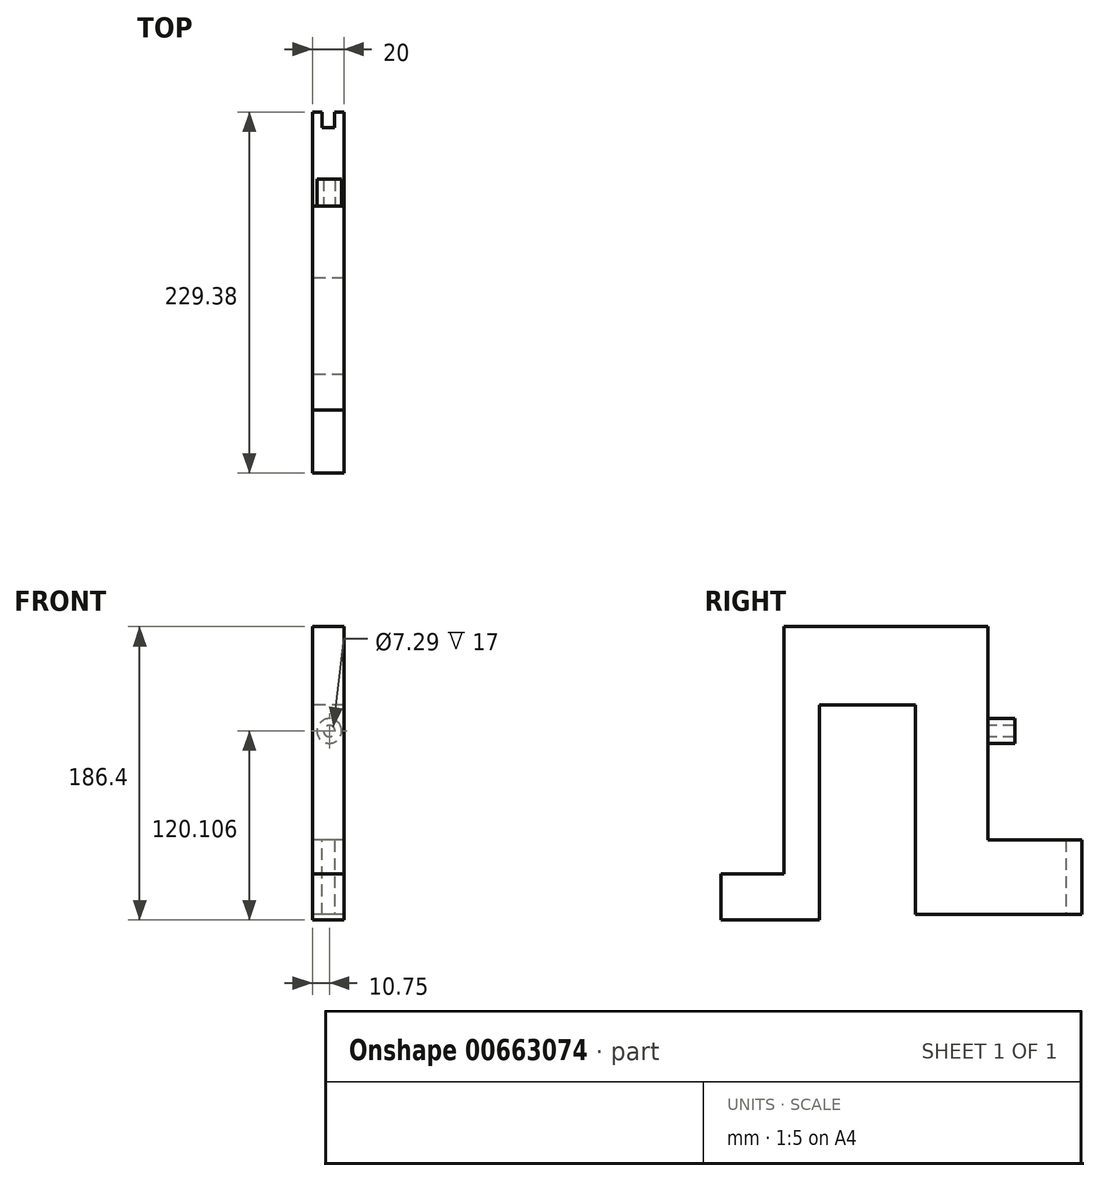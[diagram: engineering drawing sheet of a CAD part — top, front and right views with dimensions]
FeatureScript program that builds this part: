
annotation { "Feature Type Name" : "Feature", "Feature Type Description" : "" }
export const myFeature = defineFeature(function(context is Context, id is Id, definition is map)
    precondition{}
    {
        {
            var Q0;
            Q0=qCreatedBy(makeId("Right.planeOp"),FACE);
            var sketch = newSketch(context, id + "F0", { "sketchPlane" : qUnion([Q0])});
            skLineSegment(sketch, "E0", {"start": v(-81.56, -31.18) * mm, "end": v(-41.43, -31.18) * mm});
            skLineSegment(sketch, "E1", {"start": v(-41.43, -31.18) * mm, "end": v(-41.43, 125.99) * mm});
            skLineSegment(sketch, "E2", {"start": v(-41.43, 125.99) * mm, "end": v(88.2, 125.99) * mm});
            skLineSegment(sketch, "E3", {"start": v(88.2, 125.99) * mm, "end": v(88.2, -9.6) * mm});
            skLineSegment(sketch, "E4", {"start": v(88.2, -9.6) * mm, "end": v(147.82, -9.6) * mm});
            skLineSegment(sketch, "E5", {"start": v(147.82, -9.6) * mm, "end": v(147.82, -56.84) * mm});
            skLineSegment(sketch, "E6", {"start": v(147.82, -56.84) * mm, "end": v(42.17, -56.84) * mm});
            skLineSegment(sketch, "E7", {"start": v(42.17, -56.84) * mm, "end": v(42.17, 76.12) * mm});
            skLineSegment(sketch, "E8", {"start": v(42.17, 76.12) * mm, "end": v(-18.99, 76.12) * mm});
            skLineSegment(sketch, "E9", {"start": v(-18.99, 76.12) * mm, "end": v(-18.99, -60.41) * mm});
            skLineSegment(sketch, "E10", {"start": v(-18.99, -60.41) * mm, "end": v(-81.56, -60.41) * mm});
            skLineSegment(sketch, "E11", {"start": v(-81.56, -60.41) * mm, "end": v(-81.56, -31.18) * mm});
            skSolve(sketch);
        }
        {
            var Q0;
            Q0 = qSketchRegion(id + "F0", true);
            extrude(context, id + "F1", {"entities" : qUnion([Q0]), "depth" : 20 * mm, "offsetDistance" : 25 * mm});
        }
        {
            var Q0;
            Q0=makeQuery(id+"F1.opExtrude","SWEPT_FACE",FACE,{"disambiguationData":[OSD([sQuery(id+"F0.wireOp",EDGE,"E5")])]});
            var sketch = newSketch(context, id + "F2", { "sketchPlane" : qUnion([Q0])});
            skLineSegment(sketch, "E12", {"start": v(-13.93, -9.6) * mm, "end": v(-13.93, -56.84) * mm});
            skLineSegment(sketch, "E13", {"start": v(-13.93, -56.84) * mm, "end": v(-6.18, -56.84) * mm});
            skLineSegment(sketch, "E14", {"start": v(-6.18, -56.84) * mm, "end": v(-6.18, -9.6) * mm});
            skLineSegment(sketch, "E15", {"start": v(-6.18, -9.6) * mm, "end": v(-13.93, -9.6) * mm});
            skSolve(sketch);
        }
        {
            var Q0;
            Q0 = qSketchRegion(id + "F2", true);
            extrude(context, id + "F3", {"entities" : qUnion([Q0]), "operationType" : NewBodyOperationType.REMOVE, "oppositeDirection" : true, "depth" : 10 * mm, "offsetDistance" : 25 * mm});
        }
        {
            var Q0;
            Q0=makeQuery(id+"F1.opExtrude","SWEPT_FACE",FACE,{"disambiguationData":[OSD([sQuery(id+"F0.wireOp",EDGE,"E3")])]});
            var sketch = newSketch(context, id + "F4", { "sketchPlane" : qUnion([Q0])});
            skCircle(sketch, "E16", {"center": v(-10.75, 59.7) * mm, "radius": 7.85 * mm});
            skCircle(sketch, "E17", {"center": v(-10.75, 59.7) * mm, "radius": 3.64 * mm});
            skSolve(sketch);
        }
        {
            var Q0;
            Q0 = qSketchRegion(id + "F4", true);
            extrude(context, id + "F5", {"entities" : qUnion([Q0]), "operationType" : NewBodyOperationType.ADD, "depth" : 17 * mm, "offsetDistance" : 25 * mm});
        }
    });
